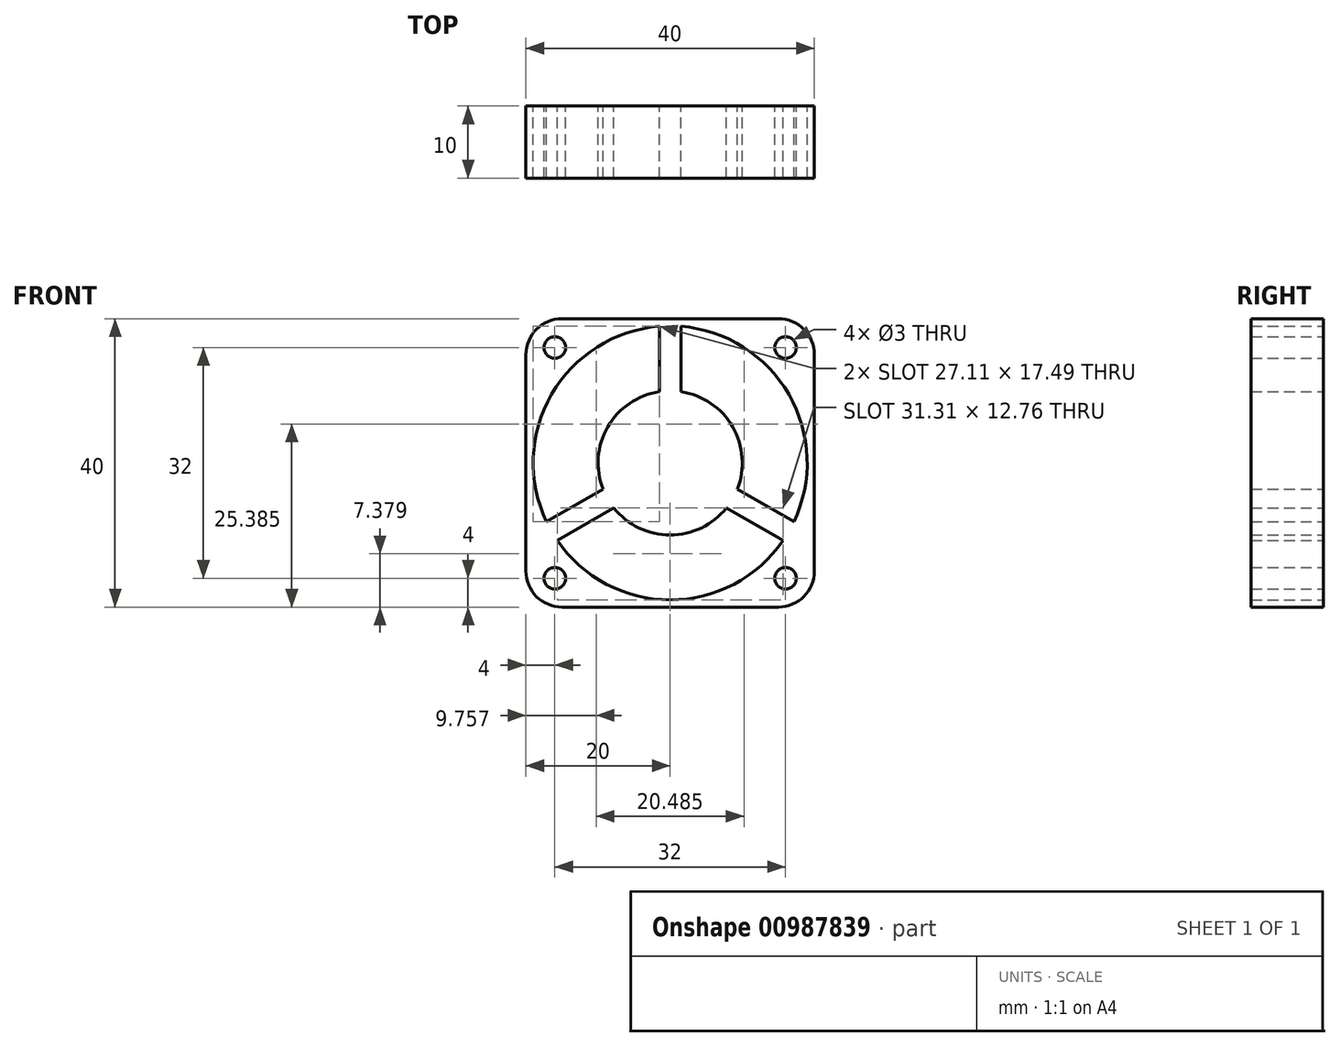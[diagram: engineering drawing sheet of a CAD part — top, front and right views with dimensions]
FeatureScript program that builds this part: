
annotation { "Feature Type Name" : "Feature", "Feature Type Description" : "" }
export const myFeature = defineFeature(function(context is Context, id is Id, definition is map)
    precondition{}
    {
        {
            var Q0;
            Q0=qCreatedBy(makeId("Front.planeOp"),FACE);
            var sketch = newSketch(context, id + "F0", { "sketchPlane" : qUnion([Q0])});
            skLineSegment(sketch, "E0.bottom", {"start": v(15, -20) * mm, "end": v(-15, -20) * mm});
            skLineSegment(sketch, "E0.top", {"start": v(15, 20) * mm, "end": v(-15, 20) * mm});
            skLineSegment(sketch, "E0.left", {"start": v(20, -15) * mm, "end": v(20, 15) * mm});
            skLineSegment(sketch, "E0.right", {"start": v(-20, -15) * mm, "end": v(-20, 15) * mm});
            skPoint(sketch, "E0.middle", {"position": v(0, 0) * mm});
            skLineSegment(sketch, "E1", {"start": v(0, 0) * mm, "end": v(20, 20) * mm, "construction": true});
            skCircle(sketch, "E2", {"center": v(16, 16) * mm, "radius": 1.5 * mm});
            skLineSegment(sketch, "E3", {"start": v(0, 0) * mm, "end": v(0, 20) * mm, "construction": true});
            skPoint(sketch, "E4.visualSharp", {"position": v(20, 20) * mm});
            skArc(sketch, "E4.filletArc", {"start": v(20, 15) * mm, "mid": v(18.54, 18.54) * mm, "end": v(15, 20) * mm});
            skPoint(sketch, "E5.visualSharp", {"position": v(20, -20) * mm});
            skArc(sketch, "E5.filletArc", {"start": v(15, -20) * mm, "mid": v(18.54, -18.54) * mm, "end": v(20, -15) * mm});
            skPoint(sketch, "E6.visualSharp", {"position": v(-20, -20) * mm});
            skArc(sketch, "E6.filletArc", {"start": v(-20, -15) * mm, "mid": v(-18.54, -18.54) * mm, "end": v(-15, -20) * mm});
            skPoint(sketch, "E7.visualSharp", {"position": v(-20, 20) * mm});
            skArc(sketch, "E7.filletArc", {"start": v(-15, 20) * mm, "mid": v(-18.54, 18.54) * mm, "end": v(-20, 15) * mm});
            skCircle(sketch, "E8.1.1", {"center": v(16, -16) * mm, "radius": 1.5 * mm});
            skLineSegment(sketch, "E8.1.2", {"start": v(-15, -20) * mm, "end": v(15, -20) * mm});
            skCircle(sketch, "E8.2.1", {"center": v(-16, -16) * mm, "radius": 1.5 * mm});
            skLineSegment(sketch, "E8.2.2", {"start": v(-20, 15) * mm, "end": v(-20, -15) * mm});
            skCircle(sketch, "E8.3.1", {"center": v(-16, 16) * mm, "radius": 1.5 * mm});
            skLineSegment(sketch, "E8.anchor1", {"start": v(0, 0) * mm, "end": v(16, 16) * mm, "construction": true});
            skLineSegment(sketch, "E8.anchor2", {"start": v(0, 0) * mm, "end": v(-16, 16) * mm, "construction": true});
            skCircle(sketch, "E9", {"center": v(0, 0) * mm, "radius": 19 * mm});
            skCircle(sketch, "E10", {"center": v(0, 0) * mm, "radius": 10 * mm});
            skLineSegment(sketch, "E11", {"start": v(-1.5, 9.89) * mm, "end": v(-1.5, 18.94) * mm});
            skLineSegment(sketch, "E12.MirrorCS", {"start": v(1.5, 9.89) * mm, "end": v(1.5, 18.94) * mm});
            skLineSegment(sketch, "E13.1.0", {"start": v(-7.81, -6.24) * mm, "end": v(-15.65, -10.77) * mm});
            skLineSegment(sketch, "E13.1.1", {"start": v(-9.31, -3.64) * mm, "end": v(-17.15, -8.17) * mm});
            skLineSegment(sketch, "E13.2.0", {"start": v(9.31, -3.64) * mm, "end": v(17.15, -8.17) * mm});
            skLineSegment(sketch, "E13.2.1", {"start": v(7.81, -6.24) * mm, "end": v(15.65, -10.77) * mm});
            skSolve(sketch);
        }
        {
            var Q0;
            Q0=makeQuery(id+"F0.imprint","IMPRINT",FACE,{"disambiguationData":[TD([[makeQuery(id+"F0.imprint","IMPRINT",EDGE,{"derivedFrom":sQuery(id+"F0.wireOp",EDGE,"E0.left")}),1.0]])]});
            var Q1;
            {var subQ0=sQuery(id+"F0.wireOp",EDGE,"E11");Q1=makeQuery(id+"F0.imprint","IMPRINT",FACE,{"disambiguationData":[TD([[makeQuery(id+"F0.imprint","IMPRINT",EDGE,{"derivedFrom":subQ0}),-1.0]])]});}
            var Q2;
            {var subQ0=sQuery(id+"F0.wireOp",EDGE,"E13.1.0");Q2=makeQuery(id+"F0.imprint","IMPRINT",FACE,{"disambiguationData":[TD([[makeQuery(id+"F0.imprint","IMPRINT",EDGE,{"derivedFrom":subQ0}),-1.0]])]});}
            var Q3;
            {var subQ0=sQuery(id+"F0.wireOp",EDGE,"E13.2.0");Q3=makeQuery(id+"F0.imprint","IMPRINT",FACE,{"disambiguationData":[TD([[makeQuery(id+"F0.imprint","IMPRINT",EDGE,{"derivedFrom":subQ0}),-1.0]])]});}
            var Q4;
            {var subQ0=sQuery(id+"F0.wireOp",EDGE,"E10");var subQ4=makeQuery(id+"F0.imprint","INTERSECT",VERTEX,{"derivedFrom":[subQ0,sQuery(id+"F0.wireOp",EDGE,"E11")]});Q4=makeQuery(id+"F0.imprint","IMPRINT",FACE,{"disambiguationData":[TD([[makeQuery(id+"F0.imprint","IMPRINT",EDGE,{"disambiguationData":[TD([[subQ4,1.0]])],"derivedFrom":subQ0}),1.0]])]});}
            extrude(context, id + "F1", {"entities" : qUnion([Q0, Q1, Q2, Q3, Q4]), "offsetDistance" : 25 * mm, "depth" : 10 * mm});
        }
    });
